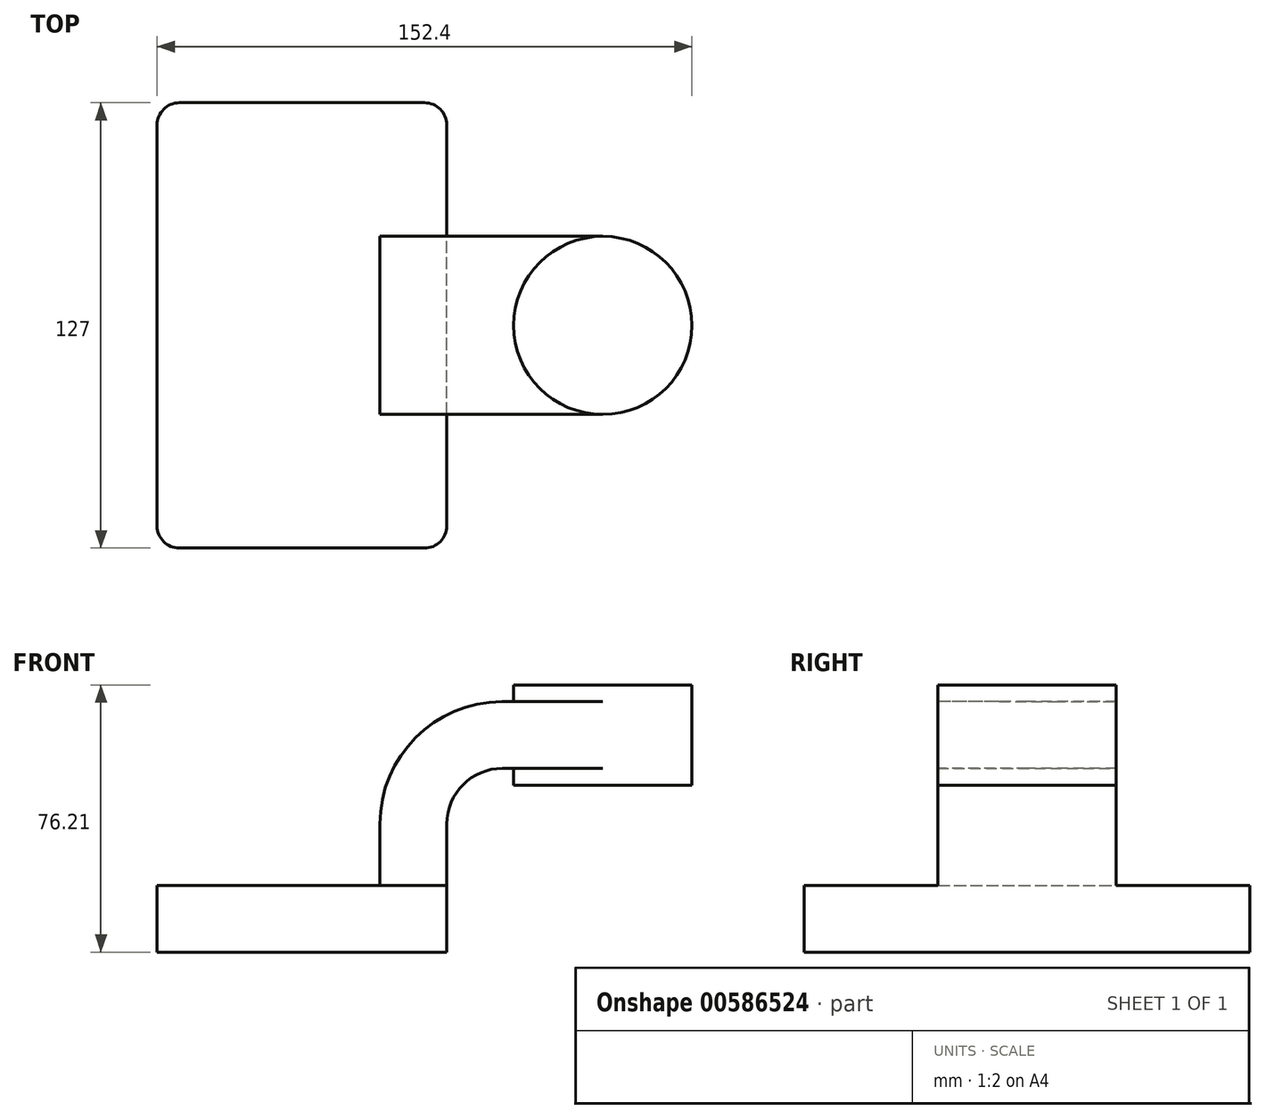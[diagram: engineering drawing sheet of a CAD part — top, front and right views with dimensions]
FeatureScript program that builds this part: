
annotation { "Feature Type Name" : "Feature", "Feature Type Description" : "" }
export const myFeature = defineFeature(function(context is Context, id is Id, definition is map)
    precondition{}
    {
        {
            var Q0;
            Q0=qCreatedBy(makeId("Front.planeOp"),FACE);
            var sketch = newSketch(context, id + "F0", { "sketchPlane" : qUnion([Q0])});
            skLineSegment(sketch, "E0.bottom", {"start": v(-41.28, 9.52) * mm, "end": v(41.28, 9.52) * mm});
            skLineSegment(sketch, "E0.top", {"start": v(-41.28, -9.52) * mm, "end": v(41.28, -9.52) * mm});
            skLineSegment(sketch, "E0.left", {"start": v(-41.27, 9.52) * mm, "end": v(-41.28, -9.52) * mm});
            skLineSegment(sketch, "E0.right", {"start": v(41.28, 9.52) * mm, "end": v(41.28, -9.52) * mm});
            skPoint(sketch, "E0.middle", {"position": v(0, 0) * mm});
            skLineSegment(sketch, "E1.bottom", {"start": v(111.13, 38.1) * mm, "end": v(60.33, 38.1) * mm});
            skLineSegment(sketch, "E1.top", {"start": v(111.13, 66.68) * mm, "end": v(60.33, 66.68) * mm});
            skLineSegment(sketch, "E1.left", {"start": v(111.13, 38.1) * mm, "end": v(111.13, 66.68) * mm});
            skLineSegment(sketch, "E1.right", {"start": v(60.33, 38.1) * mm, "end": v(60.33, 66.68) * mm});
            skPoint(sketch, "E1.middle", {"position": v(85.73, 52.39) * mm});
            skLineSegment(sketch, "E2", {"start": v(41.28, 9.52) * mm, "end": v(41.28, 27) * mm});
            skArc(sketch, "E3", {"start": v(41.28, 27) * mm, "mid": v(45.92, 38.23) * mm, "end": v(57.15, 42.88) * mm});
            skLineSegment(sketch, "E4", {"start": v(57.15, 42.88) * mm, "end": v(85.73, 42.88) * mm});
            skPoint(sketch, "E5", {"position": v(85.73, 38.1) * mm});
            skLineSegment(sketch, "E6.0", {"start": v(57.15, 61.93) * mm, "end": v(85.73, 61.93) * mm});
            skArc(sketch, "E6.1", {"start": v(22.23, 27) * mm, "mid": v(32.45, 51.7) * mm, "end": v(57.15, 61.93) * mm});
            skLineSegment(sketch, "E6.2", {"start": v(22.22, 9.52) * mm, "end": v(22.22, 27) * mm});
            skLineSegment(sketch, "E7", {"start": v(85.73, 38.1) * mm, "end": v(85.73, 66.68) * mm});
            skFitSpline(sketch, "E8", {"points": [v(-41.28, 9.52) * mm, v(57.15, 61.93) * mm], "startDerivative": vector(0.3, 73.29) * mm, "endDerivative": vector(127.63, 0.24) * mm});
            skSolve(sketch);
        }
        {
            var Q0;
            Q0=makeQuery(id+"F0.imprint","IMPRINT",FACE,{"disambiguationData":[TD([[makeQuery(id+"F0.imprint","IMPRINT",EDGE,{"derivedFrom":sQuery(id+"F0.wireOp",EDGE,"E0.top")}),1.0]])]});
            extrude(context, id + "F1", {"entities" : qUnion([Q0]), "endBound" : BoundingType.SYMMETRIC, "depth" : 127 * mm, "offsetDistance" : 25.4 * mm});
        }
        {
            var Q0;
            {var subQ5=sQuery(id+"F0.wireOp",EDGE,"E2");Q0=makeQuery(id+"F0.imprint","IMPRINT",FACE,{"disambiguationData":[TD([[makeQuery(id+"F0.imprint","IMPRINT",EDGE,{"derivedFrom":subQ5}),1.0]])]});}
            var Q1;
            {var subQ0=sQuery(id+"F0.wireOp",EDGE,"E4");var subQ1=sQuery(id+"F0.wireOp",EDGE,"E1.right");var subQ2=makeQuery(id+"F0.imprint","INTERSECT",VERTEX,{"derivedFrom":[subQ1,subQ0]});Q1=makeQuery(id+"F0.imprint","IMPRINT",FACE,{"disambiguationData":[TD([[makeQuery(id+"F0.imprint","IMPRINT",EDGE,{"disambiguationData":[TD([[subQ2,-1.0]])],"derivedFrom":subQ1}),-1.0]])]});}
            extrude(context, id + "F2", {"entities" : qUnion([Q0, Q1]), "operationType" : NewBodyOperationType.ADD, "endBound" : BoundingType.SYMMETRIC, "depth" : 50.8 * mm, "offsetDistance" : 25.4 * mm});
        }
        {
            var Q0;
            {var subQ4=sQuery(id+"F0.wireOp",EDGE,"E6.1");Q0=makeQuery(id+"F0.imprint","IMPRINT",FACE,{"disambiguationData":[TD([[makeQuery(id+"F0.imprint","IMPRINT",EDGE,{"derivedFrom":subQ4}),1.0]])]});}
            extrude(context, id + "F3", {"entities" : qUnion([Q0]), "operationType" : NewBodyOperationType.ADD, "endBound" : BoundingType.SYMMETRIC, "depth" : 15.88 * mm, "offsetDistance" : 25.4 * mm});
        }
        {
            var Q0;
            {var subQ4=sQuery(id+"F0.wireOp",EDGE,"E1.left");Q0=makeQuery(id+"F0.imprint","IMPRINT",FACE,{"disambiguationData":[TD([[makeQuery(id+"F0.imprint","IMPRINT",EDGE,{"derivedFrom":subQ4}),1.0]])]});}
            var Q1;
            Q1=sQuery(id+"F0.wireOp",EDGE,"E7");
            revolve(context, id + "F4", {"operationType" : NewBodyOperationType.ADD, "entities" : qUnion([Q0]), "axis" : qUnion([Q1]), "revolveType" : RevolveType.FULL});
        }
        {
            var Q0;
            Q0=makeQuery(id+"F1.opExtrude","CAP_EDGE",EDGE,{"disambiguationData":[OSD([sQuery(id+"F0.wireOp",EDGE,"E0.right")])],"isStart":false});
            var Q1;
            Q1=makeQuery(id+"F1.opExtrude","CAP_EDGE",EDGE,{"disambiguationData":[OSD([sQuery(id+"F0.wireOp",EDGE,"E0.left")])],"isStart":false});
            var Q2;
            Q2=makeQuery(id+"F1.opExtrude","CAP_EDGE",EDGE,{"disambiguationData":[OSD([sQuery(id+"F0.wireOp",EDGE,"E0.left")])],"isStart":true});
            var Q3;
            Q3=makeQuery(id+"F1.opExtrude","CAP_EDGE",EDGE,{"disambiguationData":[OSD([sQuery(id+"F0.wireOp",EDGE,"E0.right")])],"isStart":true});
            fillet(context, id + "F5", {"entities" : qUnion([Q0, Q1, Q2, Q3]), "radius" : 6.35 * mm, "tangentPropagation" : true, "allowEdgeOverflow" : false});
        }
    });
